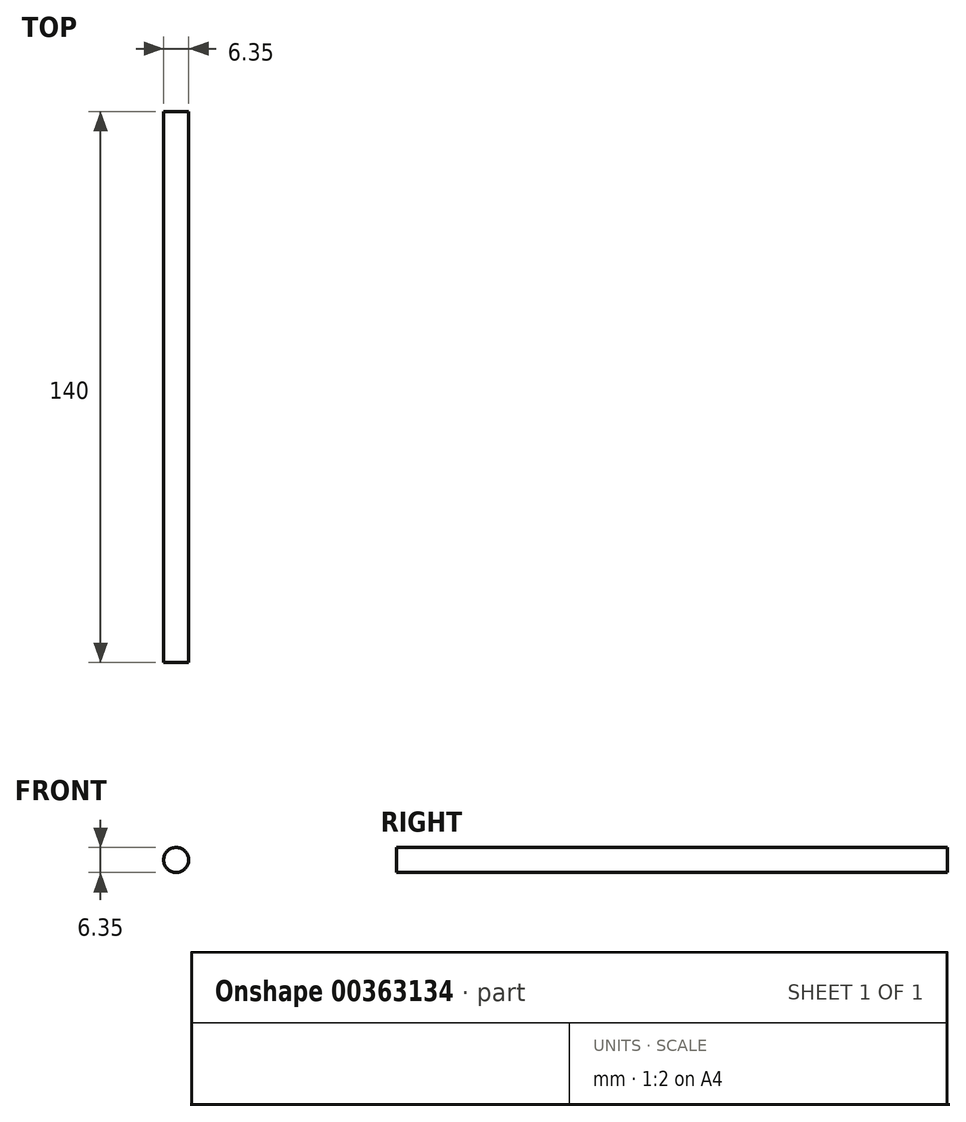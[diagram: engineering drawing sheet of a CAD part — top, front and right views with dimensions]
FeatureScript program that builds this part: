
annotation { "Feature Type Name" : "Feature", "Feature Type Description" : "" }
export const myFeature = defineFeature(function(context is Context, id is Id, definition is map)
    precondition{}
    {
        {
            var Q0;
            Q0=qCreatedBy(makeId("Front.planeOp"),FACE);
            var sketch = newSketch(context, id + "F0", { "sketchPlane" : qUnion([Q0])});
            skCircle(sketch, "E0", {"center": v(-53.93, 62.68) * mm, "radius": 3.18 * mm});
            skSolve(sketch);
        }
        {
            var Q0;
            Q0 = qSketchRegion(id + "F0", true);
            extrude(context, id + "F1", {"entities" : qUnion([Q0]), "endBound" : BoundingType.SYMMETRIC, "depth" : 140 * mm});
        }
    });
